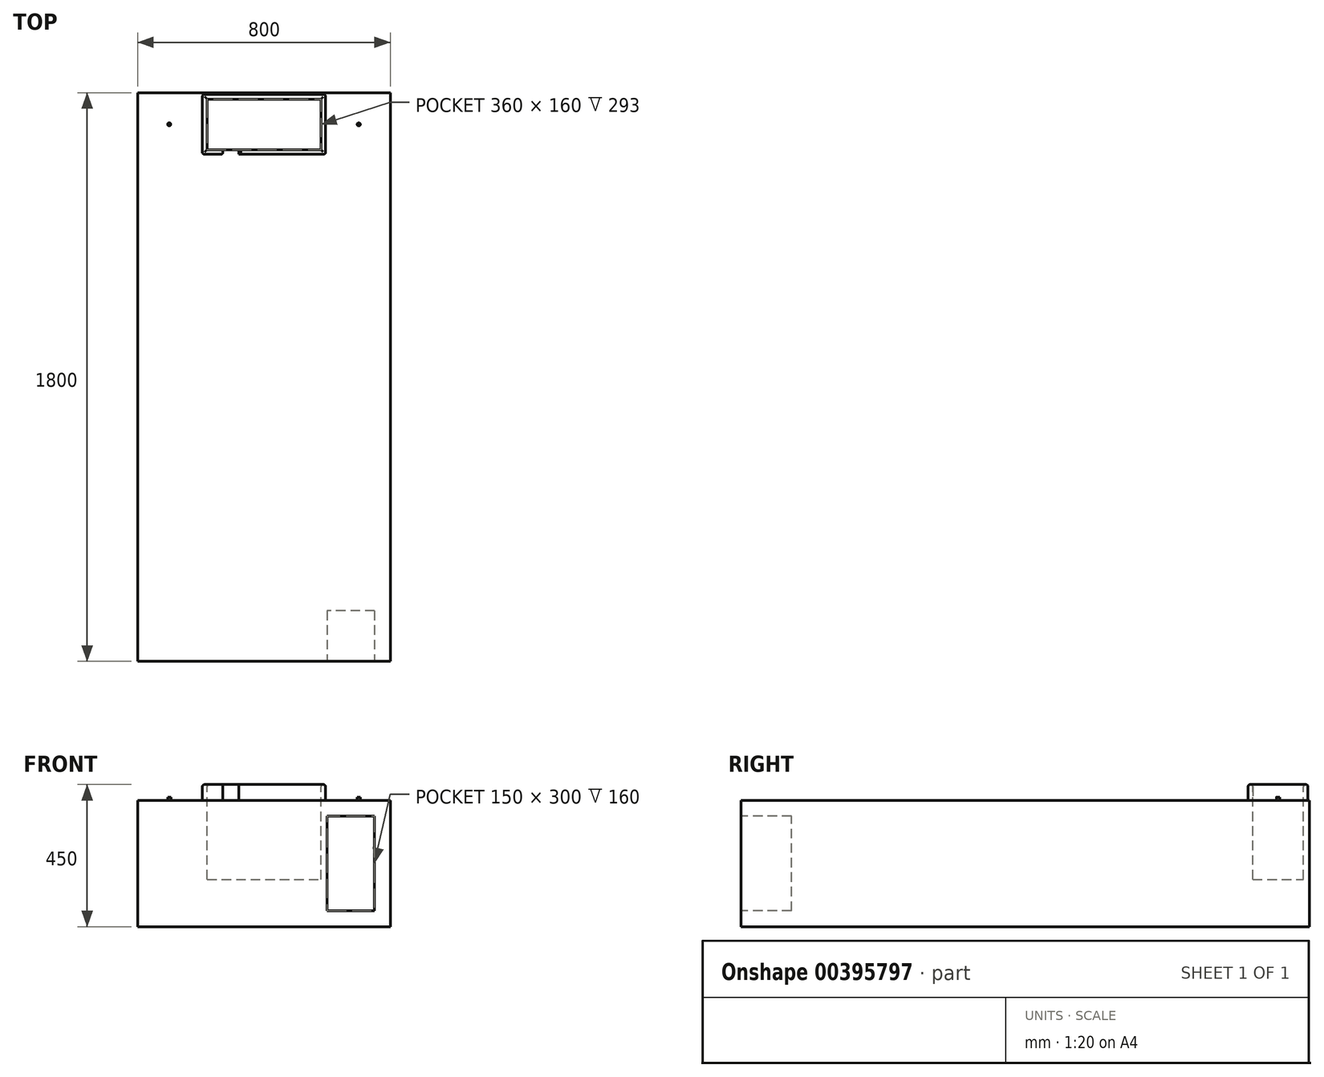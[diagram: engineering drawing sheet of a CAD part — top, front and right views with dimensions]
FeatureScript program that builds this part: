
annotation { "Feature Type Name" : "Feature", "Feature Type Description" : "" }
export const myFeature = defineFeature(function(context is Context, id is Id, definition is map)
    precondition{}
    {
        {
            var Q0;
            Q0=qCreatedBy(makeId("Top.planeOp"),FACE);
            var sketch = newSketch(context, id + "F0", { "sketchPlane" : qUnion([Q0])});
            skLineSegment(sketch, "E0.bottom", {"start": v(-400, -900) * mm, "end": v(400, -900) * mm});
            skLineSegment(sketch, "E0.top", {"start": v(-400, 900) * mm, "end": v(400, 900) * mm});
            skLineSegment(sketch, "E0.left", {"start": v(-400, -900) * mm, "end": v(-400, 900) * mm});
            skLineSegment(sketch, "E0.right", {"start": v(400, -900) * mm, "end": v(400, 900) * mm});
            skPoint(sketch, "E0.middle", {"position": v(0, 0) * mm});
            skSolve(sketch);
        }
        {
            var Q0;
            Q0=makeQuery(id+"F0.imprint","IMPRINT",FACE,{"disambiguationData":[TD([[makeQuery(id+"F0.imprint","IMPRINT",EDGE,{"derivedFrom":sQuery(id+"F0.wireOp",EDGE,"E0.bottom")}),1.0]])]});
            extrude(context, id + "F1", {"entities" : qUnion([Q0]), "depth" : 400 * mm});
        }
        {
            var Q0;
            Q0=makeQuery(id+"F1.opExtrude","CAP_FACE",FACE,{"disambiguationData":[OSD([sQuery(id+"F0.wireOp",EDGE,"E0.bottom"),sQuery(id+"F0.wireOp",EDGE,"E0.top"),sQuery(id+"F0.wireOp",EDGE,"E0.left"),sQuery(id+"F0.wireOp",EDGE,"E0.right")])],"isStart":false});
            var sketch = newSketch(context, id + "F2", { "sketchPlane" : qUnion([Q0])});
            skLineSegment(sketch, "E1.bottom", {"start": v(-400, 900) * mm, "end": v(400, 900) * mm});
            skLineSegment(sketch, "E1.top", {"start": v(-400, 700) * mm, "end": v(400, 700) * mm});
            skLineSegment(sketch, "E1.left", {"start": v(-400, 900) * mm, "end": v(-400, 700) * mm});
            skLineSegment(sketch, "E1.right", {"start": v(400, 900) * mm, "end": v(400, 700) * mm});
            skLineSegment(sketch, "E2", {"start": v(0, 700) * mm, "end": v(0, 900) * mm});
            skLineSegment(sketch, "E3.bottom", {"start": v(-180, 720) * mm, "end": v(180, 720) * mm});
            skLineSegment(sketch, "E3.top", {"start": v(-180, 880) * mm, "end": v(180, 880) * mm});
            skLineSegment(sketch, "E3.left", {"start": v(-180, 720) * mm, "end": v(-180, 880) * mm});
            skLineSegment(sketch, "E3.right", {"start": v(180, 720) * mm, "end": v(180, 880) * mm});
            skPoint(sketch, "E3.middle", {"position": v(0, 800) * mm});
            skLineSegment(sketch, "E4.0", {"start": v(-195, 705) * mm, "end": v(-195, 895) * mm});
            skLineSegment(sketch, "E4.1", {"start": v(-195, 705) * mm, "end": v(195, 705) * mm});
            skLineSegment(sketch, "E4.2", {"start": v(195, 705) * mm, "end": v(195, 895) * mm});
            skLineSegment(sketch, "E4.3", {"start": v(-195, 895) * mm, "end": v(195, 895) * mm});
            skLineSegment(sketch, "E5", {"start": v(-130, 720) * mm, "end": v(-130, 705) * mm});
            skLineSegment(sketch, "E6", {"start": v(-80, 720) * mm, "end": v(-80, 705) * mm});
            skCircle(sketch, "E7", {"center": v(300, 800) * mm, "radius": 5 * mm});
            skPoint(sketch, "E7.centerSnap0", {"position": v(400, 800) * mm});
            skCircle(sketch, "E8", {"center": v(-300, 800) * mm, "radius": 5 * mm});
            skPoint(sketch, "E8.centerSnap0", {"position": v(-400, 800) * mm});
            skSolve(sketch);
        }
        {
            var Q0;
            {var subQ5=sQuery(id+"F2.wireOp",EDGE,"E3.left");Q0=makeQuery(id+"F2.imprint","IMPRINT",FACE,{"disambiguationData":[TD([[makeQuery(id+"F2.imprint","IMPRINT",EDGE,{"derivedFrom":subQ5}),-1.0]])]});}
            var Q1;
            {var subQ5=sQuery(id+"F2.wireOp",EDGE,"E3.right");Q1=makeQuery(id+"F2.imprint","IMPRINT",FACE,{"disambiguationData":[TD([[makeQuery(id+"F2.imprint","IMPRINT",EDGE,{"derivedFrom":subQ5}),1.0]])]});}
            extrude(context, id + "F3", {"entities" : qUnion([Q0, Q1]), "operationType" : NewBodyOperationType.REMOVE, "oppositeDirection" : true, "depth" : 250 * mm});
        }
        {
            var Q0;
            {var subQ0=sQuery(id+"F2.wireOp",EDGE,"E3.left");Q0=makeQuery(id+"F2.imprint","IMPRINT",FACE,{"disambiguationData":[TD([[makeQuery(id+"F2.imprint","IMPRINT",EDGE,{"derivedFrom":subQ0}),1.0]])]});}
            var Q1;
            {var subQ0=sQuery(id+"F2.wireOp",EDGE,"E3.right");Q1=makeQuery(id+"F2.imprint","IMPRINT",FACE,{"disambiguationData":[TD([[makeQuery(id+"F2.imprint","IMPRINT",EDGE,{"derivedFrom":subQ0}),-1.0]])]});}
            var Q2;
            {var subQ5=sQuery(id+"F2.wireOp",EDGE,"E6");Q2=makeQuery(id+"F2.imprint","IMPRINT",FACE,{"disambiguationData":[TD([[makeQuery(id+"F2.imprint","IMPRINT",EDGE,{"derivedFrom":subQ5}),1.0]])]});}
            extrude(context, id + "F4", {"entities" : qUnion([Q0, Q1, Q2]), "operationType" : NewBodyOperationType.ADD, "depth" : 50 * mm});
        }
        {
            var Q0;
            Q0=makeQuery(id+"F4.opExtrude","CAP_FACE",FACE,{"disambiguationData":[OSD([sQuery(id+"F2.wireOp",EDGE,"E3.bottom"),sQuery(id+"F2.wireOp",EDGE,"E3.top"),sQuery(id+"F2.wireOp",EDGE,"E3.left"),sQuery(id+"F2.wireOp",EDGE,"E3.right"),sQuery(id+"F2.wireOp",EDGE,"E4.0"),sQuery(id+"F2.wireOp",EDGE,"E4.1"),sQuery(id+"F2.wireOp",EDGE,"E4.2"),sQuery(id+"F2.wireOp",EDGE,"E4.3")])],"isStart":false});
            var Q1;
            Q1=makeQuery(id+"F4.opExtrude","SWEPT_EDGE",EDGE,{"disambiguationData":[OSD([sQuery(id+"F2.wireOp",EDGE,"E4.1"),sQuery(id+"F2.wireOp",EDGE,"E5")])]});
            var Q2;
            Q2=makeQuery(id+"F4.opExtrude","SWEPT_EDGE",EDGE,{"disambiguationData":[OSD([sQuery(id+"F2.wireOp",EDGE,"E3.bottom"),sQuery(id+"F2.wireOp",EDGE,"E5")])]});
            var Q3;
            Q3=makeQuery(id+"F4.opExtrude","SWEPT_EDGE",EDGE,{"disambiguationData":[OSD([sQuery(id+"F2.wireOp",EDGE,"E4.0"),sQuery(id+"F2.wireOp",EDGE,"E4.1")])]});
            var Q4;
            Q4=makeQuery(id+"F4.opExtrude","SWEPT_EDGE",EDGE,{"disambiguationData":[OSD([sQuery(id+"F2.wireOp",EDGE,"E4.1"),sQuery(id+"F2.wireOp",EDGE,"E4.2")])]});
            var Q5;
            Q5=makeQuery(id+"F4.opExtrude","SWEPT_EDGE",EDGE,{"disambiguationData":[OSD([sQuery(id+"F2.wireOp",EDGE,"E4.2"),sQuery(id+"F2.wireOp",EDGE,"E4.3")])]});
            var Q6;
            Q6=makeQuery(id+"F4.opExtrude","SWEPT_EDGE",EDGE,{"disambiguationData":[OSD([sQuery(id+"F2.wireOp",EDGE,"E4.0"),sQuery(id+"F2.wireOp",EDGE,"E4.3")])]});
            fillet(context, id + "F5", {"entities" : qUnion([Q0, Q1, Q2, Q3, Q4, Q5, Q6]), "radius" : 7 * mm, "tangentPropagation" : true, "allowEdgeOverflow" : false});
        }
        {
            var Q0;
            Q0=makeQuery(id+"F2.imprint","IMPRINT",FACE,{"disambiguationData":[TD([[makeQuery(id+"F2.imprint","IMPRINT",EDGE,{"derivedFrom":sQuery(id+"F2.wireOp",EDGE,"E8")}),1.0]])]});
            var Q1;
            Q1=makeQuery(id+"F2.imprint","IMPRINT",FACE,{"disambiguationData":[TD([[makeQuery(id+"F2.imprint","IMPRINT",EDGE,{"derivedFrom":sQuery(id+"F2.wireOp",EDGE,"E7")}),1.0]])]});
            extrude(context, id + "F6", {"entities" : qUnion([Q0, Q1]), "operationType" : NewBodyOperationType.ADD, "depth" : 10 * mm});
        }
        {
            var Q0;
            Q0=makeQuery(id+"F1.opExtrude","SWEPT_FACE",FACE,{"disambiguationData":[OSD([sQuery(id+"F0.wireOp",EDGE,"E0.bottom")])]});
            var sketch = newSketch(context, id + "F7", { "sketchPlane" : qUnion([Q0])});
            skLineSegment(sketch, "E9.bottom", {"start": v(350, 50) * mm, "end": v(200, 50) * mm});
            skLineSegment(sketch, "E9.top", {"start": v(350, 350) * mm, "end": v(200, 350) * mm});
            skLineSegment(sketch, "E9.left", {"start": v(350, 50) * mm, "end": v(350, 350) * mm});
            skLineSegment(sketch, "E9.right", {"start": v(200, 50) * mm, "end": v(200, 350) * mm});
            skSolve(sketch);
        }
        {
            var Q0;
            Q0=makeQuery(id+"F7.imprint","IMPRINT",FACE,{"disambiguationData":[TD([[makeQuery(id+"F7.imprint","IMPRINT",EDGE,{"derivedFrom":sQuery(id+"F7.wireOp",EDGE,"E9.bottom")}),-1.0]])]});
            extrude(context, id + "F8", {"entities" : qUnion([Q0]), "operationType" : NewBodyOperationType.REMOVE, "oppositeDirection" : true, "depth" : 160 * mm});
        }
    });
